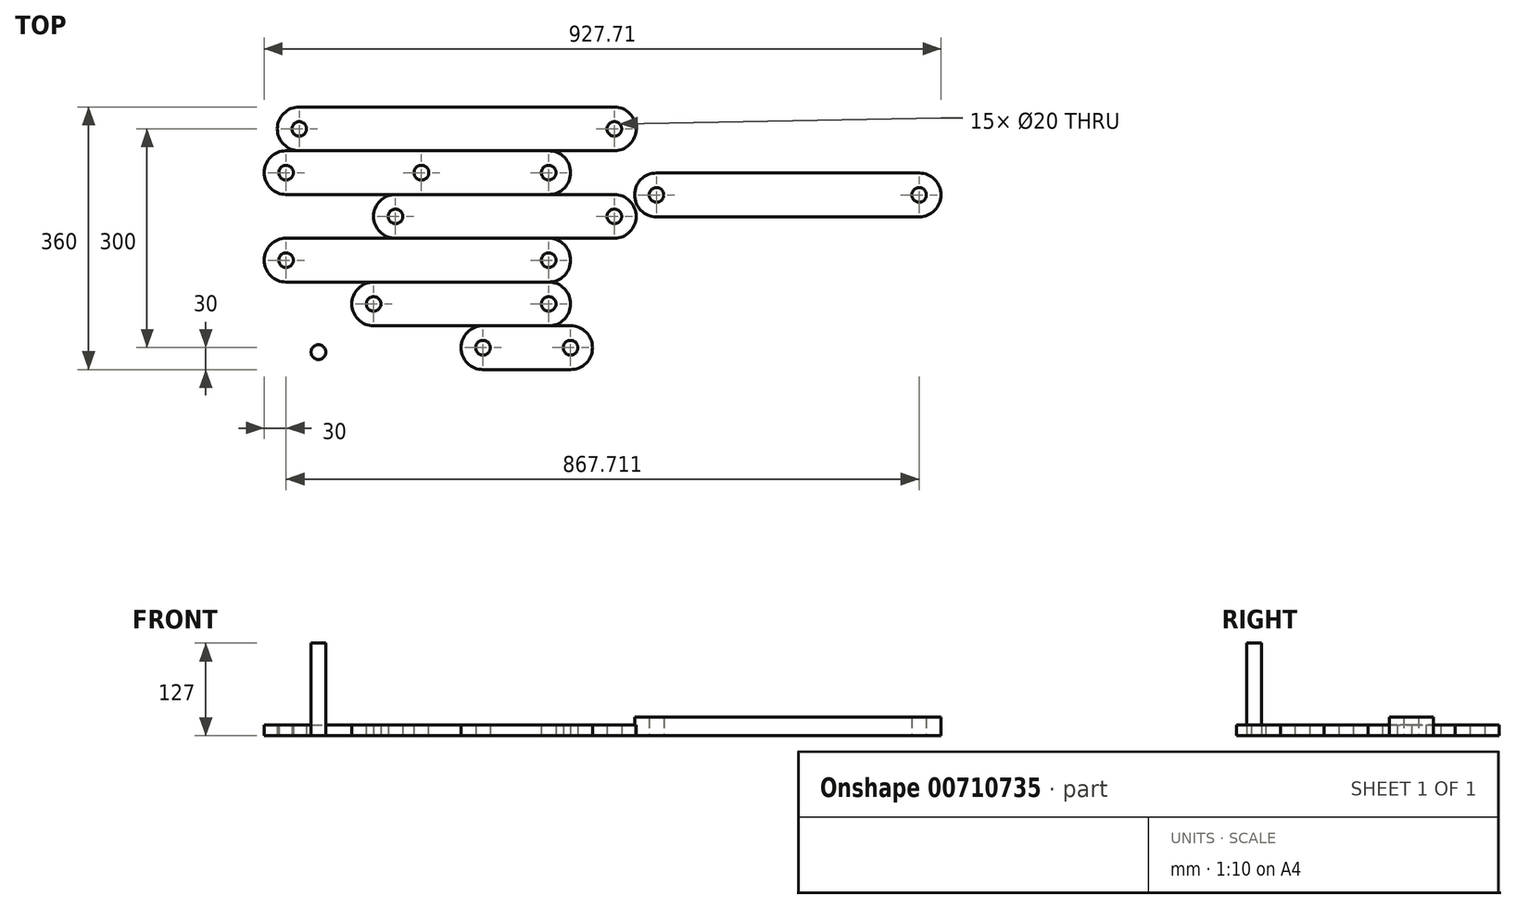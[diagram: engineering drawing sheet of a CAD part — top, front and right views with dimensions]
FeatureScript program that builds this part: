
annotation { "Feature Type Name" : "Feature", "Feature Type Description" : "" }
export const myFeature = defineFeature(function(context is Context, id is Id, definition is map)
    precondition{}
    {
        {
            var Q0;
            Q0=qCreatedBy(makeId("Top.planeOp"),FACE);
            var sketch = newSketch(context, id + "F0", { "sketchPlane" : qUnion([Q0])});
            skCircle(sketch, "E0", {"center": v(0, 0) * mm, "radius": 10 * mm});
            skArc(sketch, "E1", {"start": v(0, 30) * mm, "mid": v(-30, 0) * mm, "end": v(0, -30) * mm});
            skLineSegment(sketch, "E2", {"start": v(0, 30) * mm, "end": v(120, 30) * mm});
            skLineSegment(sketch, "E3", {"start": v(0, -30) * mm, "end": v(120, -30) * mm});
            skArc(sketch, "E4", {"start": v(120, -30) * mm, "mid": v(150, 0) * mm, "end": v(120, 30) * mm});
            skCircle(sketch, "E5", {"center": v(120, 0) * mm, "radius": 10 * mm});
            skSolve(sketch);
        }
        {
            var Q0;
            Q0=makeQuery(id+"F0.imprint","IMPRINT",FACE,{"disambiguationData":[TD([[makeQuery(id+"F0.imprint","IMPRINT",EDGE,{"derivedFrom":sQuery(id+"F0.wireOp",EDGE,"E0")}),-1.0]])]});
            extrude(context, id + "F1", {"entities" : qUnion([Q0]), "depth" : 15 * mm});
        }
        {
            var Q0;
            Q0=qCreatedBy(makeId("Top.planeOp"),FACE);
            var sketch = newSketch(context, id + "F2", { "sketchPlane" : qUnion([Q0])});
            skCircle(sketch, "E6", {"center": v(-150, 0) * mm, "radius": 10 * mm});
            skArc(sketch, "E7", {"start": v(-150, 30) * mm, "mid": v(-180, 0) * mm, "end": v(-150, -30) * mm});
            skLineSegment(sketch, "E8", {"start": v(-150, 30) * mm, "end": v(90, 30) * mm});
            skLineSegment(sketch, "E9", {"start": v(-150, -30) * mm, "end": v(90, -30) * mm});
            skArc(sketch, "E10", {"start": v(90, -30) * mm, "mid": v(120, 0) * mm, "end": v(90, 30) * mm});
            skCircle(sketch, "E11", {"center": v(90, 0) * mm, "radius": 10 * mm});
            skSolve(sketch);
        }
        {
            var Q0;
            Q0=makeQuery(id+"F2.imprint","IMPRINT",FACE,{"disambiguationData":[TD([[makeQuery(id+"F2.imprint","IMPRINT",EDGE,{"derivedFrom":sQuery(id+"F2.wireOp",EDGE,"E6")}),-1.0]])]});
            extrude(context, id + "F3", {"entities" : qUnion([Q0]), "depth" : 15 * mm});
        }
        {
            var Q0;
            Q0=makeQuery(id+"F3.opExtrude","SWEPT_BODY",BODY,{"disambiguationData":[OSD([sQuery(id+"F2.wireOp",EDGE,"E6"),sQuery(id+"F2.wireOp",EDGE,"E7"),sQuery(id+"F2.wireOp",EDGE,"E8"),sQuery(id+"F2.wireOp",EDGE,"E9"),sQuery(id+"F2.wireOp",EDGE,"E10"),sQuery(id+"F2.wireOp",EDGE,"E11")])]});
            transform(context, id + "F4", {"entities" : qUnion([Q0]), "transformType" : TransformType.TRANSLATION_3D, "dx" : 0 * mm, "dy" : 60 * mm, "dz" : 0 * mm, "makeCopy" : false});
        }
        {
            var Q0;
            Q0=qCreatedBy(makeId("Top.planeOp"),FACE);
            var sketch = newSketch(context, id + "F5", { "sketchPlane" : qUnion([Q0])});
            skCircle(sketch, "E12", {"center": v(-270, 0) * mm, "radius": 10 * mm});
            skArc(sketch, "E13", {"start": v(-270, 30) * mm, "mid": v(-300, 0) * mm, "end": v(-270, -30) * mm});
            skLineSegment(sketch, "E14", {"start": v(-270, 30) * mm, "end": v(90, 30) * mm});
            skLineSegment(sketch, "E15", {"start": v(-270, -30) * mm, "end": v(90, -30) * mm});
            skArc(sketch, "E16", {"start": v(90, -30) * mm, "mid": v(120, 0) * mm, "end": v(90, 30) * mm});
            skCircle(sketch, "E17", {"center": v(90, 0) * mm, "radius": 10 * mm});
            skSolve(sketch);
        }
        {
            var Q0;
            Q0=makeQuery(id+"F5.imprint","IMPRINT",FACE,{"disambiguationData":[TD([[makeQuery(id+"F5.imprint","IMPRINT",EDGE,{"derivedFrom":sQuery(id+"F5.wireOp",EDGE,"E12")}),-1.0]])]});
            extrude(context, id + "F6", {"entities" : qUnion([Q0]), "depth" : 15 * mm});
        }
        {
            var Q0;
            Q0=makeQuery(id+"F6.opExtrude","SWEPT_BODY",BODY,{"disambiguationData":[OSD([sQuery(id+"F5.wireOp",EDGE,"E12"),sQuery(id+"F5.wireOp",EDGE,"E13"),sQuery(id+"F5.wireOp",EDGE,"E14"),sQuery(id+"F5.wireOp",EDGE,"E15"),sQuery(id+"F5.wireOp",EDGE,"E16"),sQuery(id+"F5.wireOp",EDGE,"E17")])]});
            transform(context, id + "F7", {"entities" : qUnion([Q0]), "transformType" : TransformType.TRANSLATION_3D, "dx" : 0 * mm, "dy" : 120 * mm, "dz" : 0 * mm, "makeCopy" : false});
        }
        {
            var Q0;
            Q0=qCreatedBy(makeId("Top.planeOp"),FACE);
            var sketch = newSketch(context, id + "F8", { "sketchPlane" : qUnion([Q0])});
            skCircle(sketch, "E18", {"center": v(-120, 0) * mm, "radius": 10 * mm});
            skArc(sketch, "E19", {"start": v(-120, 30) * mm, "mid": v(-150, 0) * mm, "end": v(-120, -30) * mm});
            skLineSegment(sketch, "E20", {"start": v(-120, 30) * mm, "end": v(180, 30) * mm});
            skLineSegment(sketch, "E21", {"start": v(-120, -30) * mm, "end": v(180, -30) * mm});
            skArc(sketch, "E22", {"start": v(180, -30) * mm, "mid": v(210, 0) * mm, "end": v(180, 30) * mm});
            skCircle(sketch, "E23", {"center": v(180, 0) * mm, "radius": 10 * mm});
            skSolve(sketch);
        }
        {
            var Q0;
            Q0=makeQuery(id+"F8.imprint","IMPRINT",FACE,{"disambiguationData":[TD([[makeQuery(id+"F8.imprint","IMPRINT",EDGE,{"derivedFrom":sQuery(id+"F8.wireOp",EDGE,"E18")}),-1.0]])]});
            extrude(context, id + "F9", {"entities" : qUnion([Q0]), "depth" : 15 * mm});
        }
        {
            var Q0;
            Q0=makeQuery(id+"F9.opExtrude","SWEPT_BODY",BODY,{"disambiguationData":[OSD([sQuery(id+"F8.wireOp",EDGE,"E18"),sQuery(id+"F8.wireOp",EDGE,"E19"),sQuery(id+"F8.wireOp",EDGE,"E20"),sQuery(id+"F8.wireOp",EDGE,"E21"),sQuery(id+"F8.wireOp",EDGE,"E22"),sQuery(id+"F8.wireOp",EDGE,"E23")])]});
            transform(context, id + "F10", {"entities" : qUnion([Q0]), "transformType" : TransformType.TRANSLATION_3D, "dx" : 0 * mm, "dy" : 180 * mm, "dz" : 0 * mm, "makeCopy" : false});
        }
        {
            var Q0;
            Q0=qCreatedBy(makeId("Top.planeOp"),FACE);
            var sketch = newSketch(context, id + "F11", { "sketchPlane" : qUnion([Q0])});
            skCircle(sketch, "E24", {"center": v(-225.6, -5.99) * mm, "radius": 10.14 * mm});
            skSolve(sketch);
        }
        {
            var Q0;
            Q0=makeQuery(id+"F11.imprint","IMPRINT",FACE,{"disambiguationData":[TD([[makeQuery(id+"F11.imprint","IMPRINT",EDGE,{"derivedFrom":sQuery(id+"F11.wireOp",EDGE,"E24")}),1.0]])]});
            extrude(context, id + "F12", {"entities" : qUnion([Q0]), "depth" : 127 * mm, "offsetDistance" : 25.4 * mm});
        }
        {
            var Q0;
            Q0=makeQuery(id+"F6.opExtrude","SWEPT_BODY",BODY,{"disambiguationData":[OSD([sQuery(id+"F5.wireOp",EDGE,"E12"),sQuery(id+"F5.wireOp",EDGE,"E13"),sQuery(id+"F5.wireOp",EDGE,"E14"),sQuery(id+"F5.wireOp",EDGE,"E15"),sQuery(id+"F5.wireOp",EDGE,"E16"),sQuery(id+"F5.wireOp",EDGE,"E17")])]});
            transform(context, id + "F13", {"entities" : qUnion([Q0]), "transformType" : TransformType.TRANSLATION_3D, "dx" : 0 * mm, "dy" : 120 * mm, "dz" : 0 * mm, "makeCopy" : true});
        }
        {
            var Q0;
            Q0=makeQuery(id+"F13.opPattern","COPY",FACE,{"derivedFrom":makeQuery(id+"F6.opExtrude","CAP_FACE",FACE,{"disambiguationData":[OSD([sQuery(id+"F5.wireOp",EDGE,"E12"),sQuery(id+"F5.wireOp",EDGE,"E13"),sQuery(id+"F5.wireOp",EDGE,"E14"),sQuery(id+"F5.wireOp",EDGE,"E15"),sQuery(id+"F5.wireOp",EDGE,"E16"),sQuery(id+"F5.wireOp",EDGE,"E17")])],"isStart":false}),"instanceName":"1"});
            var sketch = newSketch(context, id + "F14", { "sketchPlane" : qUnion([Q0])});
            skCircle(sketch, "E25", {"center": v(-84.43, 240) * mm, "radius": 10 * mm});
            skSolve(sketch);
        }
        {
            var Q0;
            Q0=makeQuery(id+"F14.imprint","IMPRINT",FACE,{"disambiguationData":[TD([[makeQuery(id+"F14.imprint","IMPRINT",EDGE,{"derivedFrom":sQuery(id+"F14.wireOp",EDGE,"E25")}),1.0]])]});
            extrude(context, id + "F15", {"entities" : qUnion([Q0]), "operationType" : NewBodyOperationType.REMOVE, "endBound" : BoundingType.THROUGH_ALL, "oppositeDirection" : true, "depth" : 25 * mm});
        }
        {
            var Q0;
            Q0=qCreatedBy(makeId("Top.planeOp"),FACE);
            var sketch = newSketch(context, id + "F16", { "sketchPlane" : qUnion([Q0])});
            skCircle(sketch, "E26", {"center": v(-252, 0) * mm, "radius": 10 * mm});
            skArc(sketch, "E27", {"start": v(-252, 30) * mm, "mid": v(-282, 0) * mm, "end": v(-252, -30) * mm});
            skLineSegment(sketch, "E28", {"start": v(-252, 30) * mm, "end": v(180, 30) * mm});
            skLineSegment(sketch, "E29", {"start": v(-252, -30) * mm, "end": v(180, -30) * mm});
            skArc(sketch, "E30", {"start": v(180, -30) * mm, "mid": v(210, 0) * mm, "end": v(180, 30) * mm});
            skCircle(sketch, "E31", {"center": v(180, 0) * mm, "radius": 10 * mm});
            skSolve(sketch);
        }
        {
            var Q0;
            Q0=qSketchRegion(id+"F16",true);
            extrude(context, id + "F17", {"entities" : qUnion([Q0]), "depth" : 15 * mm});
        }
        {
            var Q0;
            Q0=makeQuery(id+"F17.opExtrude","SWEPT_BODY",BODY,{"disambiguationData":[OSD([sQuery(id+"F16.wireOp",EDGE,"E26"),sQuery(id+"F16.wireOp",EDGE,"E27"),sQuery(id+"F16.wireOp",EDGE,"E28"),sQuery(id+"F16.wireOp",EDGE,"E29"),sQuery(id+"F16.wireOp",EDGE,"E30"),sQuery(id+"F16.wireOp",EDGE,"E31")])]});
            transform(context, id + "F18", {"entities" : qUnion([Q0]), "transformType" : TransformType.TRANSLATION_3D, "dx" : 0 * mm, "dy" : 300 * mm, "dz" : 0 * mm, "makeCopy" : false});
        }
        {
            var Q0;
            Q0=qCreatedBy(makeId("Top.planeOp"),FACE);
            var sketch = newSketch(context, id + "F19", { "sketchPlane" : qUnion([Q0])});
            skCircle(sketch, "E32", {"center": v(237.71, 209.5) * mm, "radius": 10 * mm});
            skArc(sketch, "E33", {"start": v(237.71, 239.5) * mm, "mid": v(207.71, 209.5) * mm, "end": v(237.71, 179.5) * mm});
            skLineSegment(sketch, "E34", {"start": v(237.71, 239.5) * mm, "end": v(597.71, 239.5) * mm});
            skLineSegment(sketch, "E35", {"start": v(237.71, 179.5) * mm, "end": v(597.71, 179.5) * mm});
            skArc(sketch, "E36", {"start": v(597.71, 179.5) * mm, "mid": v(627.71, 209.5) * mm, "end": v(597.71, 239.5) * mm});
            skCircle(sketch, "E37", {"center": v(597.71, 209.5) * mm, "radius": 10 * mm});
            skSolve(sketch);
        }
        {
            var Q0;
            Q0=qSketchRegion(id+"F19",true);
            extrude(context, id + "F20", {"entities" : qUnion([Q0]), "depth" : 25.4 * mm, "offsetDistance" : 25.4 * mm});
        }
    });
